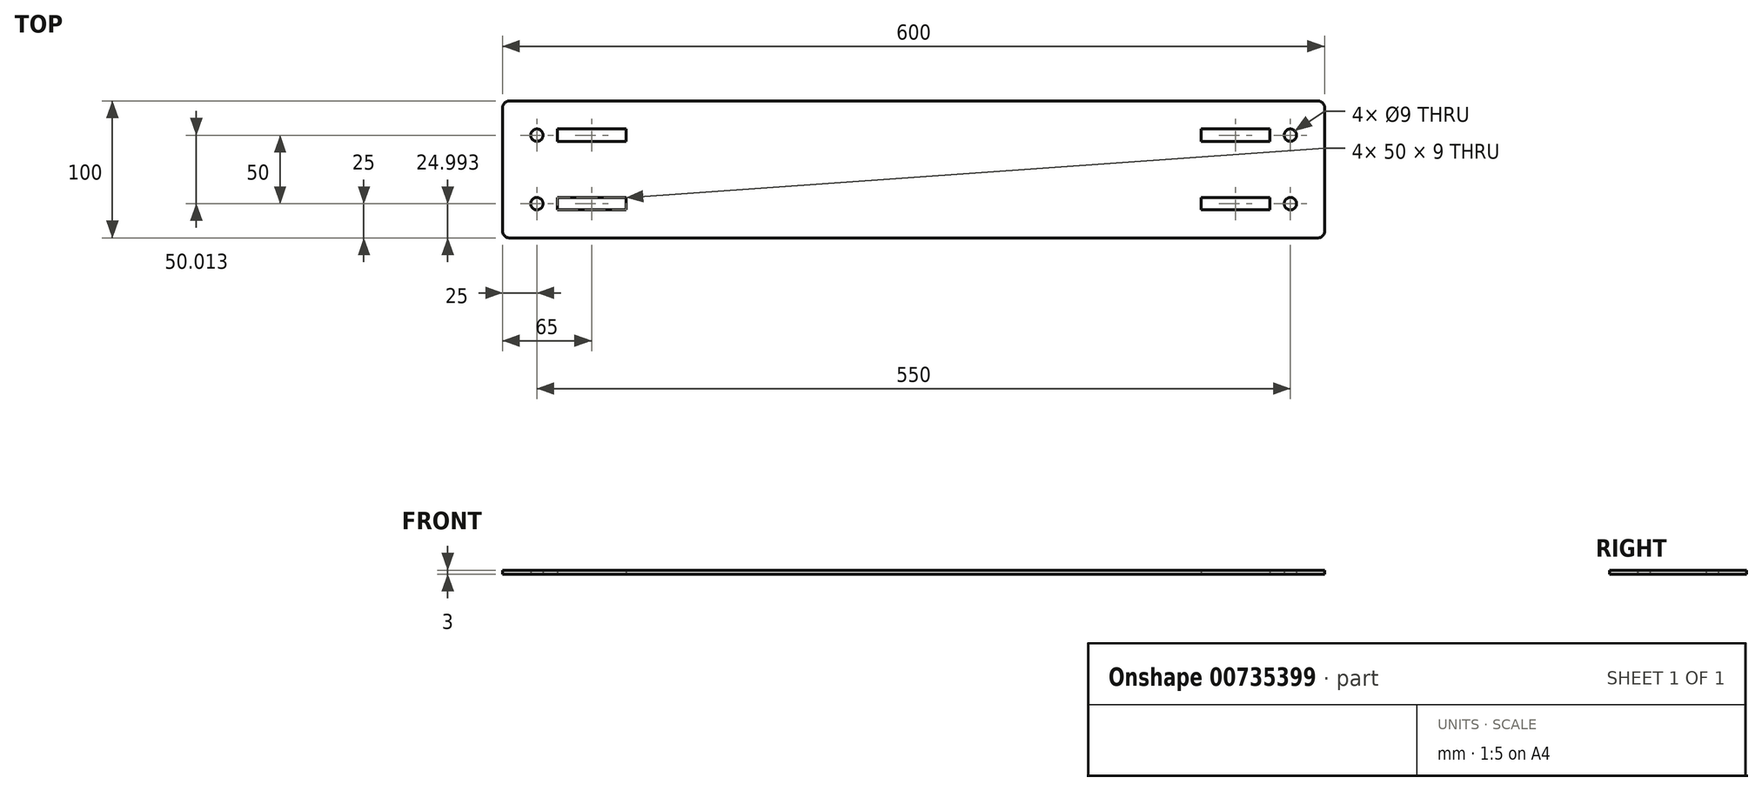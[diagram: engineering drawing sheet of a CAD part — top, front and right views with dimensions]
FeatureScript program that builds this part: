
annotation { "Feature Type Name" : "Feature", "Feature Type Description" : "" }
export const myFeature = defineFeature(function(context is Context, id is Id, definition is map)
    precondition{}
    {
        {
            var Q0;
            Q0=qCreatedBy(makeId("Top.planeOp"),FACE);
            var sketch = newSketch(context, id + "F0", { "sketchPlane" : qUnion([Q0])});
            skLineSegment(sketch, "E0.bottom", {"start": v(-5, 0) * mm, "end": v(-595, 0) * mm});
            skLineSegment(sketch, "E0.top", {"start": v(-5, -100) * mm, "end": v(-595, -100) * mm});
            skLineSegment(sketch, "E0.left", {"start": v(0, -5) * mm, "end": v(0, -95) * mm});
            skLineSegment(sketch, "E0.right", {"start": v(-600, -5) * mm, "end": v(-600, -95) * mm});
            skPoint(sketch, "E1.startSnap0", {"position": v(-300, 0) * mm});
            skPoint(sketch, "E2.visualSharp", {"position": v(-600, 0) * mm});
            skArc(sketch, "E2.filletArc", {"start": v(-595, 0) * mm, "mid": v(-598.54, -1.46) * mm, "end": v(-600, -5) * mm});
            skPoint(sketch, "E3.visualSharp", {"position": v(-600, -100) * mm});
            skArc(sketch, "E3.filletArc", {"start": v(-600, -95) * mm, "mid": v(-598.54, -98.54) * mm, "end": v(-595, -100) * mm});
            skPoint(sketch, "E4.visualSharp", {"position": v(0, 0) * mm});
            skArc(sketch, "E4.filletArc", {"start": v(0, -5) * mm, "mid": v(-1.46, -1.46) * mm, "end": v(-5, 0) * mm});
            skPoint(sketch, "E5.visualSharp", {"position": v(0, -100) * mm});
            skArc(sketch, "E5.filletArc", {"start": v(-5, -100) * mm, "mid": v(-1.46, -98.54) * mm, "end": v(0, -95) * mm});
            skPoint(sketch, "E6.startSnap0", {"position": v(-600, -50) * mm});
            skCircle(sketch, "E7", {"center": v(-575, -25) * mm, "radius": 4.5 * mm});
            skCircle(sketch, "E8.MirrorC", {"center": v(-575, -75) * mm, "radius": 4.5 * mm});
            skCircle(sketch, "E9.MirrorC", {"center": v(-25, -25) * mm, "radius": 4.5 * mm});
            skCircle(sketch, "E10.MirrorC", {"center": v(-25, -75) * mm, "radius": 4.5 * mm});
            skLineSegment(sketch, "E11", {"start": v(-550, 0) * mm, "end": v(-550, -3) * mm});
            skLineSegment(sketch, "E12.MirrorCS", {"start": v(-550, -100) * mm, "end": v(-550, -97) * mm});
            skLineSegment(sketch, "E13.MirrorCS", {"start": v(-50, 0) * mm, "end": v(-50, -3) * mm});
            skLineSegment(sketch, "E14.MirrorCS", {"start": v(-50, -100) * mm, "end": v(-50, -97) * mm});
            skLineSegment(sketch, "E15", {"start": v(-300, -50) * mm, "end": v(-300, -48) * mm});
            skLineSegment(sketch, "E16", {"start": v(-300, -50) * mm, "end": v(-302, -50) * mm});
            skLineSegment(sketch, "E17.MirrorCS", {"start": v(-300, -50) * mm, "end": v(-300, -52) * mm});
            skLineSegment(sketch, "E18.MirrorCS", {"start": v(-300, -50) * mm, "end": v(-298, -50) * mm});
            skLineSegment(sketch, "E19", {"start": v(-300, 13.6) * mm, "end": v(-300, -107.4) * mm, "construction": true});
            skLineSegment(sketch, "E20.bottom", {"start": v(-560, -20.5) * mm, "end": v(-510, -20.5) * mm});
            skLineSegment(sketch, "E20.top", {"start": v(-560, -29.5) * mm, "end": v(-510, -29.5) * mm});
            skLineSegment(sketch, "E20.left", {"start": v(-560, -20.5) * mm, "end": v(-560, -29.5) * mm});
            skLineSegment(sketch, "E20.right", {"start": v(-510, -20.5) * mm, "end": v(-510, -29.5) * mm});
            skLineSegment(sketch, "E21.MirrorCS", {"start": v(-510, -79.5) * mm, "end": v(-510, -70.5) * mm});
            skLineSegment(sketch, "E22.MirrorCS", {"start": v(-560, -79.5) * mm, "end": v(-510, -79.5) * mm});
            skLineSegment(sketch, "E23.MirrorCS", {"start": v(-560, -70.5) * mm, "end": v(-510, -70.5) * mm});
            skLineSegment(sketch, "E24.MirrorCS", {"start": v(-560, -79.5) * mm, "end": v(-560, -70.5) * mm});
            skLineSegment(sketch, "E25.MirrorCS", {"start": v(-90, -20.5) * mm, "end": v(-90, -29.5) * mm});
            skLineSegment(sketch, "E26.MirrorCS", {"start": v(-40, -20.5) * mm, "end": v(-40, -29.5) * mm});
            skLineSegment(sketch, "E27.MirrorCS", {"start": v(-90, -79.5) * mm, "end": v(-90, -70.5) * mm});
            skLineSegment(sketch, "E28.MirrorCS", {"start": v(-40, -79.5) * mm, "end": v(-40, -70.5) * mm});
            skLineSegment(sketch, "E29.MirrorCS", {"start": v(-40, -79.5) * mm, "end": v(-90, -79.5) * mm});
            skLineSegment(sketch, "E30.MirrorCS", {"start": v(-40, -29.5) * mm, "end": v(-90, -29.5) * mm});
            skLineSegment(sketch, "E31.MirrorCS", {"start": v(-40, -70.5) * mm, "end": v(-90, -70.5) * mm});
            skLineSegment(sketch, "E32.MirrorCS", {"start": v(-40, -20.5) * mm, "end": v(-90, -20.5) * mm});
            skSolve(sketch);
        }
        {
            var Q0;
            Q0=makeQuery(id+"F0.imprint","IMPRINT",FACE,{"disambiguationData":[TD([[makeQuery(id+"F0.imprint","IMPRINT",EDGE,{"derivedFrom":sQuery(id+"F0.wireOp",EDGE,"E0.left")}),-1.0]])]});
            extrude(context, id + "F1", {"entities" : qUnion([Q0]), "depth" : 3 * mm, "offsetDistance" : 25 * mm});
        }
    });
